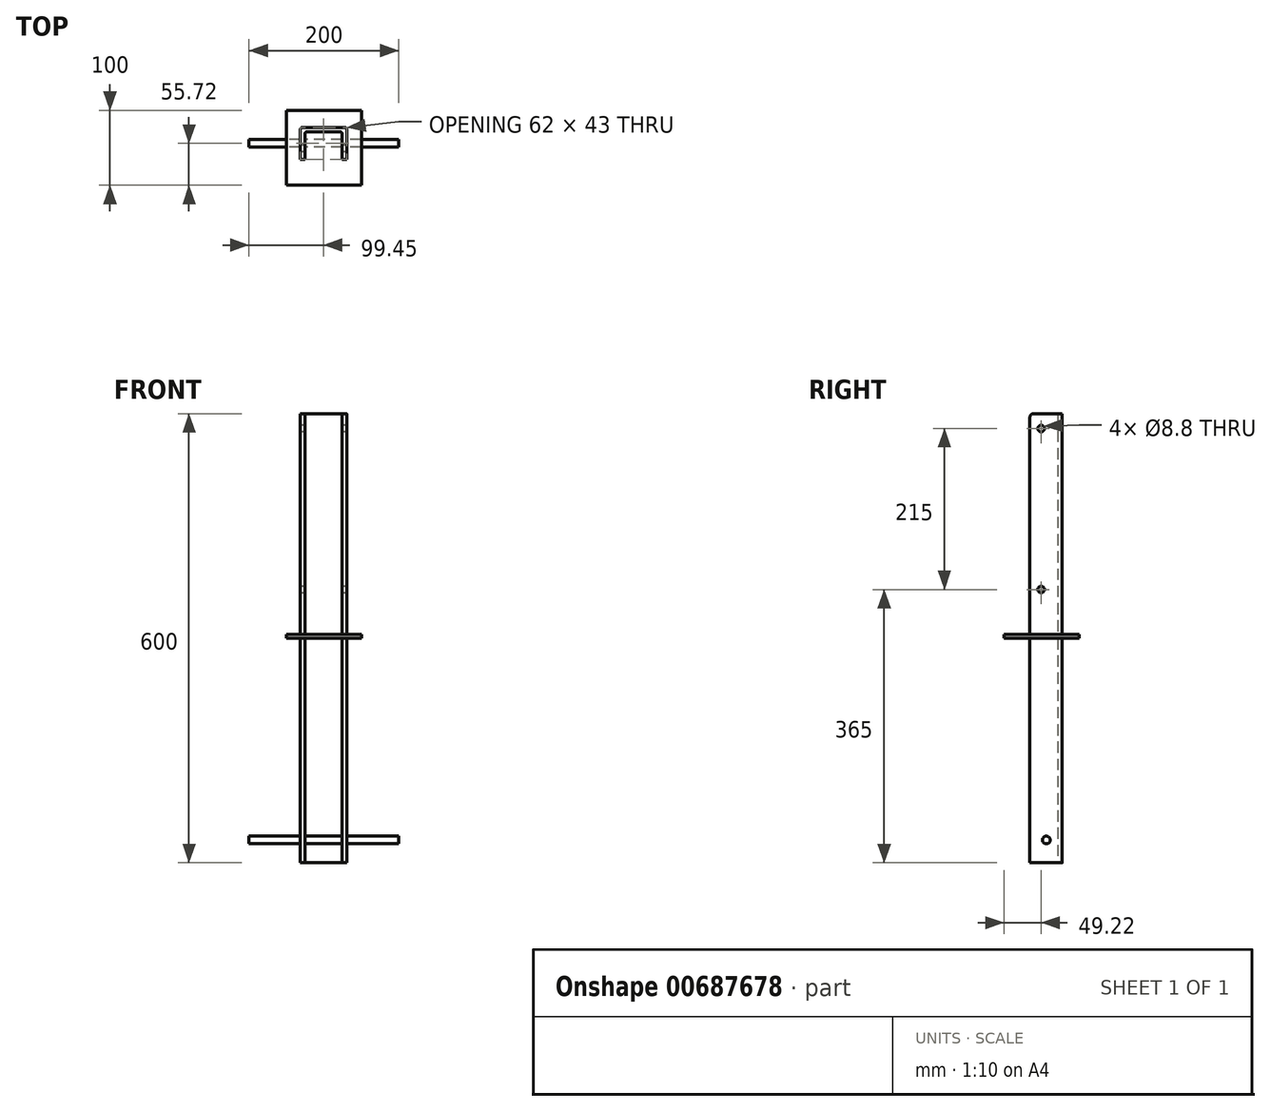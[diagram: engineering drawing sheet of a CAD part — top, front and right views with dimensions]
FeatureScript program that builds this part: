
annotation { "Feature Type Name" : "Feature", "Feature Type Description" : "" }
export const myFeature = defineFeature(function(context is Context, id is Id, definition is map)
    precondition{}
    {
        {
            var Q0;
            Q0=qCreatedBy(makeId("Top.planeOp"),FACE);
            var sketch = newSketch(context, id + "F0", { "sketchPlane" : qUnion([Q0])});
            skLineSegment(sketch, "E0", {"start": v(-25.55, -15.78) * mm, "end": v(-25.55, 18.22) * mm});
            skLineSegment(sketch, "E1", {"start": v(-22.55, 21.22) * mm, "end": v(21.45, 21.22) * mm});
            skLineSegment(sketch, "E2", {"start": v(24.45, 18.22) * mm, "end": v(24.45, -15.78) * mm});
            skLineSegment(sketch, "E3.0", {"start": v(30.45, 24.22) * mm, "end": v(30.45, -15.78) * mm});
            skLineSegment(sketch, "E3.1", {"start": v(-28.55, 27.22) * mm, "end": v(27.45, 27.22) * mm});
            skLineSegment(sketch, "E3.2", {"start": v(-31.55, -15.78) * mm, "end": v(-31.55, 24.22) * mm});
            skLineSegment(sketch, "E4", {"start": v(30.45, -15.78) * mm, "end": v(24.45, -15.78) * mm});
            skLineSegment(sketch, "E5", {"start": v(-25.55, -15.78) * mm, "end": v(-31.55, -15.78) * mm});
            skPoint(sketch, "E6.visualSharp", {"position": v(-25.55, 21.22) * mm});
            skArc(sketch, "E6.filletArc", {"start": v(-22.55, 21.22) * mm, "mid": v(-24.67, 20.34) * mm, "end": v(-25.55, 18.22) * mm});
            skPoint(sketch, "E7.visualSharp", {"position": v(24.45, 21.22) * mm});
            skArc(sketch, "E7.filletArc", {"start": v(24.45, 18.22) * mm, "mid": v(23.57, 20.34) * mm, "end": v(21.45, 21.22) * mm});
            skPoint(sketch, "E8.visualSharp", {"position": v(-31.55, 27.22) * mm});
            skArc(sketch, "E8.filletArc", {"start": v(-28.55, 27.22) * mm, "mid": v(-30.67, 26.34) * mm, "end": v(-31.55, 24.22) * mm});
            skPoint(sketch, "E9.visualSharp", {"position": v(30.45, 27.22) * mm});
            skArc(sketch, "E9.filletArc", {"start": v(30.45, 24.22) * mm, "mid": v(29.57, 26.34) * mm, "end": v(27.45, 27.22) * mm});
            skSolve(sketch);
        }
        {
            var Q0;
            Q0=makeQuery(id+"F0.imprint","IMPRINT",FACE,{"disambiguationData":[TD([[makeQuery(id+"F0.imprint","IMPRINT",EDGE,{"derivedFrom":sQuery(id+"F0.wireOp",EDGE,"E0")}),1.0]])]});
            extrude(context, id + "F1", {"entities" : qUnion([Q0]), "endBound" : BoundingType.SYMMETRIC, "depth" : 600 * mm, "offsetDistance" : 25 * mm});
        }
        {
            var Q0;
            Q0=qCreatedBy(makeId("Top.planeOp"),FACE);
            var sketch = newSketch(context, id + "F2", { "sketchPlane" : qUnion([Q0])});
            skLineSegment(sketch, "E10.bottom", {"start": v(-50, 50) * mm, "end": v(50, 50) * mm});
            skLineSegment(sketch, "E10.top", {"start": v(-50, -50) * mm, "end": v(50, -50) * mm});
            skLineSegment(sketch, "E10.left", {"start": v(-50, 50) * mm, "end": v(-50, -50) * mm});
            skLineSegment(sketch, "E10.right", {"start": v(50, 50) * mm, "end": v(50, -50) * mm});
            skPoint(sketch, "E10.middle", {"position": v(0, 0) * mm});
            skSolve(sketch);
        }
        {
            var Q0;
            Q0 = qSketchRegion(id + "F2", true);
            extrude(context, id + "F3", {"entities" : qUnion([Q0]), "operationType" : NewBodyOperationType.ADD, "depth" : 5 * mm, "offsetDistance" : 25 * mm});
        }
        {
            var Q0;
            {var subQ2=sQuery(id+"F0.wireOp",EDGE,"E3.2");Q0=makeQuery(id+"F3.boolean.opBoolean","SPLIT",FACE,{"disambiguationData":[TD([makeQuery(id+"F3.opExtrude","CAP_FACE",FACE,{"disambiguationData":[OSD([sQuery(id+"F2.wireOp",EDGE,"E10.bottom"),sQuery(id+"F2.wireOp",EDGE,"E10.top"),sQuery(id+"F2.wireOp",EDGE,"E10.left"),sQuery(id+"F2.wireOp",EDGE,"E10.right")])],"isStart":false})])],"derivedFrom":makeQuery(id+"F1.opExtrude","SWEPT_FACE",FACE,{"disambiguationData":[OSD([subQ2])]})});}
            var sketch = newSketch(context, id + "F4", { "sketchPlane" : qUnion([Q0])});
            skPoint(sketch, "E11", {"position": v(0.78, 65) * mm});
            skPoint(sketch, "E12", {"position": v(0.78, 280) * mm});
            skSolve(sketch);
        }
        {
            var Q0;
            Q0=sQuery(id+"F4.wireOp",VERTEX,"E12");
            var Q1;
            Q1=sQuery(id+"F4.wireOp",VERTEX,"E11");
            var Q2;
            Q2=makeQuery(id+"F1.opExtrude","SWEPT_BODY",BODY,{"disambiguationData":[OSD([sQuery(id+"F0.wireOp",EDGE,"E0"),sQuery(id+"F0.wireOp",EDGE,"E1"),sQuery(id+"F0.wireOp",EDGE,"E2"),sQuery(id+"F0.wireOp",EDGE,"E3.0"),sQuery(id+"F0.wireOp",EDGE,"E3.1"),sQuery(id+"F0.wireOp",EDGE,"E3.2"),sQuery(id+"F0.wireOp",EDGE,"E4"),sQuery(id+"F0.wireOp",EDGE,"E5"),sQuery(id+"F0.wireOp",EDGE,"E6.filletArc"),sQuery(id+"F0.wireOp",EDGE,"E7.filletArc"),sQuery(id+"F0.wireOp",EDGE,"E8.filletArc"),sQuery(id+"F0.wireOp",EDGE,"E9.filletArc")])]});
            hole(context, id + "F5", {"style" : HoleStyle.SIMPLE, "endStyle" : HoleEndStyle.THROUGH, "standardTappedOrClearance" : lookupTablePath({ "standard" : "ISO", "fit" : "Normal", "size" : "M8", "type" : "Clearance" }), "standardBlindInLast" : lookupTablePath({ "fit" : "Standard", "standard" : "ISO", "size" : "M8", "type" : "Clearance" }), "holeDiameter" : 8.8 * mm, "majorDiameter" : 5 * mm, "isTappedThrough" : true, "tappedDepth" : 12 * mm, "tapClearance" : 3, "locations" : qUnion([Q0, Q1]), "scope" : qUnion([Q2])});
        }
        {
            var Q0;
            Q0=makeQuery(id+"F1.opExtrude","CAP_EDGE",EDGE,{"disambiguationData":[OSD([sQuery(id+"F0.wireOp",EDGE,"E5")])],"isStart":false});
            var Q1;
            Q1=makeQuery(id+"F1.opExtrude","CAP_EDGE",EDGE,{"disambiguationData":[OSD([sQuery(id+"F0.wireOp",EDGE,"E4")])],"isStart":false});
            fillet(context, id + "F6", {"entities" : qUnion([Q0, Q1]), "radius" : 5 * mm, "tangentPropagation" : true, "allowEdgeOverflow" : false});
        }
        {
            var Q0;
            Q0=qCreatedBy(makeId("Right.planeOp"),FACE);
            var sketch = newSketch(context, id + "F7", { "sketchPlane" : qUnion([Q0])});
            skCircle(sketch, "E13", {"center": v(6.07, -269.52) * mm, "radius": 5.12 * mm});
            skSolve(sketch);
        }
        {
            var Q0;
            Q0 = qSketchRegion(id + "F7", true);
            extrude(context, id + "F8", {"entities" : qUnion([Q0]), "operationType" : NewBodyOperationType.ADD, "endBound" : BoundingType.SYMMETRIC, "depth" : 200 * mm, "offsetDistance" : 25 * mm});
        }
    });
